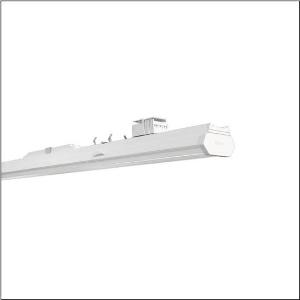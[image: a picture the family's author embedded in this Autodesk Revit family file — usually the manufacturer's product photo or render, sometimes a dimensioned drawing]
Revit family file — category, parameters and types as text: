
# Revit family: licross_11_protected_ho_51tp13mn4gxs
name_source: partatom
category: Lighting Fixtures
units: mm (PartAtom-declared; Revit-internal decimal feet)

## family parameters
Cut with Voids When Loaded = No
Host = Face
Light Source = No
Part Type = Normal
Room Calculation Point = No
Round Connector Dimension = Use Diameter
Shared = No

## types (1)
- --- (1 x LED, 16110 lm, 87.4 W, 4000K)
    Apparent Load = 87 VA
    CIE Flux Codes = 89 96 99 100 99
    Color Rendering = 80
    Color Temperature = 4000K
    Default Elevation = 1800 mm
    Description = Licross 11 Protected HO, luminaire insert, of sheet steel, galvanised, coil coated, white, length: 1.500mm, width: 90mm, height: 101mm, LED rated luminous flux: 16.110lm, light colour: 840, SDCM (Standard Deviation of Colour Matching)MacAdam ≤ 2 SDCM (initial), control gear: ON/OFF Multilumen, with plug, 3-pole, with phase selection, mains connection: 220..240V, AC, 50/60Hz, rated input power: 87W, internal wiring halogen-free, primary light control with lens, of plastic, primary optical cover: cover, of PMMA, light emission: direct distribution, primary light characteristic: symmetric, protection rating (complete): IP64, insulation class (complete): insulation class I (protective earthing), certification: CE, ENEC, VDE, UKCA, protection symbol: D if used in an environment with conductive dust loads with corresponding accessories, impact resistance: IK06, permissible ambient temperature for indoor applications: -35..+35°C, corresponds to IFS (International Featured Standards) requirements for safety and quality in the food industry, reducing of maximum allowable ambient temperature of 5°C with ceiling mounting, LABS conformity tested according to VDMA 24364:2018-05, The light source and the operating device comply with the requirements of the Ecodesign Regulation (EU) 2019/2020 and are replaceable in accordance with this regulation, packaging unit: 1 piece
    Height = 92 mm
    Lamp = 1 x LED
    Lamp Light Flux = 16110 lm
    Lamp Power = 87.4 W
    Lamp count = 1
    Length = 1500 mm
    Luminous efficacy = 184 lm/W
    Manufacturer = Siteco
    ModVariant = No
    Model = 51TP13MN4GXS
    Mounting Place = Ceiling
    Mounting Type = Pendant
    Number of Poles = 1
    OnlyDefault = Yes
    Power Factor = 1
    Product Name = Licross 11 Protected HO
    Product group = luminaire insert | ceiling pendant
    ProductGroupID = 901
    Protection Class = Protection class I
    Protection Degree = IP 64
    RLX_Detail_Level = 1
    RLX_Emergency_Light_Flux = 0 lm
    RLX_Emergency_Type = 0
    RLX_Emergency_Type_DB = No
    RlxData = <blob elided: 22309 chars, md5=cc60053c>
    Socket = socket
    Standby Power = 0 W
    System Light Flux = 16110 lm
    System Power = 87 W
    Type Comments = factory setting: luminous flux: 100 % | (A | C | E) | 203 mA
    Type Image = l_1256148.jpg
    URL = http://relux.com
    VarID = @adj_091909
    Voltage = 0 V
    Weight = 0.00 kg
    Width = 88 mm

## geometry (parser evidence)
native form markers: Blend x4, Sweep x11
no freeform markers — native parametric forms only
